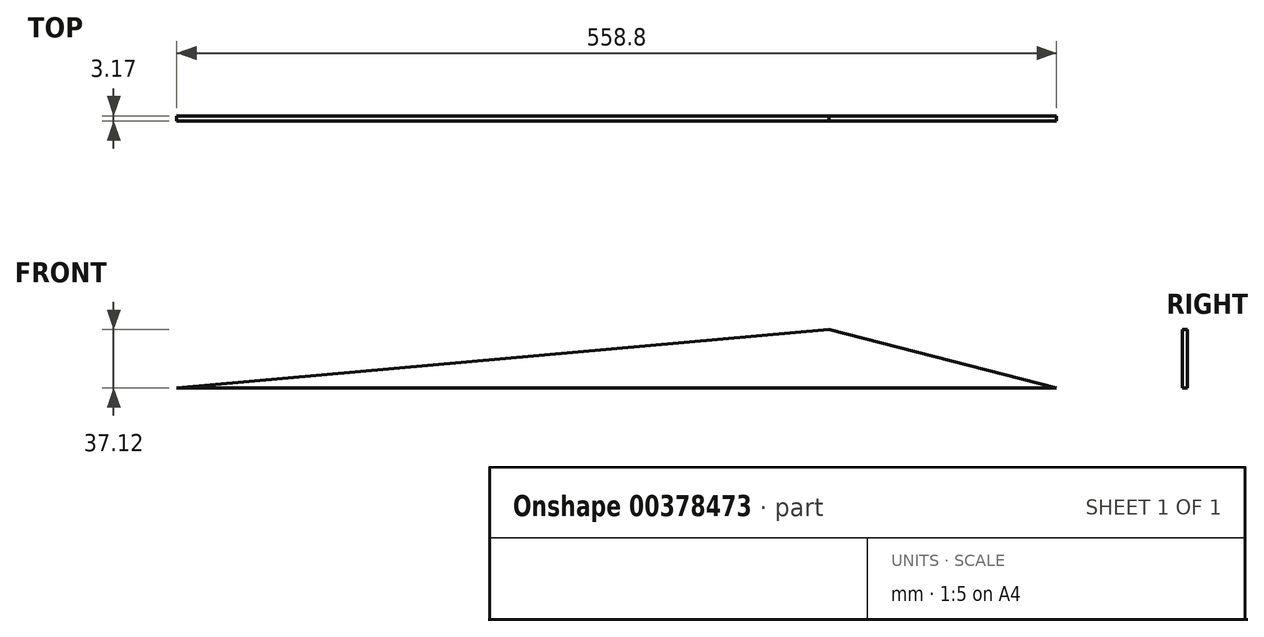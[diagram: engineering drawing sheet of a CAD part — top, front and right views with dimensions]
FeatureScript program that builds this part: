
annotation { "Feature Type Name" : "Feature", "Feature Type Description" : "" }
export const myFeature = defineFeature(function(context is Context, id is Id, definition is map)
    precondition{}
    {
        {
            var Q0;
            Q0=qCreatedBy(makeId("Front.planeOp"),FACE);
            var sketch = newSketch(context, id + "F0", { "sketchPlane" : qUnion([Q0])});
            skLineSegment(sketch, "E0", {"start": v(-281.9, 0) * mm, "end": v(276.9, 0) * mm});
            skLineSegment(sketch, "E1", {"start": v(276.9, 0) * mm, "end": v(132.36, 37.12) * mm});
            skLineSegment(sketch, "E2", {"start": v(132.36, 37.12) * mm, "end": v(-281.9, 0) * mm});
            skSolve(sketch);
        }
        {
            var Q0;
            Q0 = qSketchRegion(id + "F0", true);
            extrude(context, id + "F1", {"entities" : qUnion([Q0]), "depth" : 3.17 * mm});
        }
    });
